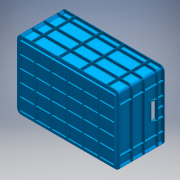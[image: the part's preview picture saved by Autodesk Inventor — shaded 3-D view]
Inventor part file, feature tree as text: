
AUTODESK INVENTOR PART (.ipt)
format: ipt  version: 2016 (Build 200138000, 138)  size: 743,936 bytes
history: native  units: mm
features: other x1, extrude x1
ambient origin geometry x8: Origin, YZ Plane, XZ Plane, XY Plane, X Axis, Y Axis, Z Axis, Center Point
bodies: Body1 (feature_tree)
feature tree (2):
  other  "Sólido1"
  extrude  "Extrude14"  [1 undecoded]
note: 1 required parameter value undecoded (feature->parameter linkage not recoverable at this tier; creation-order binding heuristic only, values carry confidence <= 0.55)
